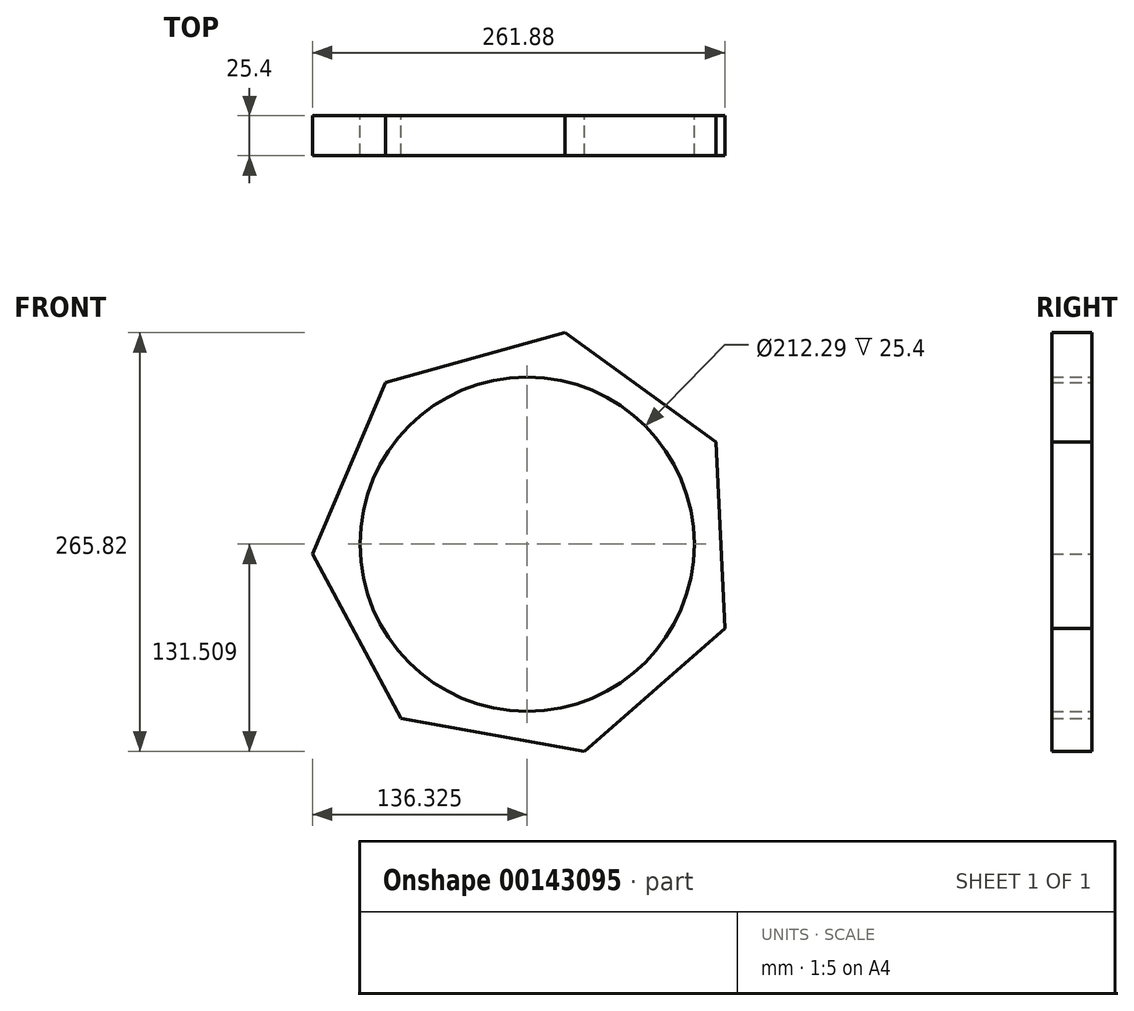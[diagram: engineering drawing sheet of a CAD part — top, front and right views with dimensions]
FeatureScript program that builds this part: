
annotation { "Feature Type Name" : "Feature", "Feature Type Description" : "" }
export const myFeature = defineFeature(function(context is Context, id is Id, definition is map)
    precondition{}
    {
        {
            var Q0;
            Q0=qCreatedBy(makeId("Front.planeOp"),FACE);
            var sketch = newSketch(context, id + "F0", { "sketchPlane" : qUnion([Q0])});
            skCircle(sketch, "E0.cCircle", {"center": v(148.42, -19.18) * mm, "radius": 122.96 * mm, "construction": true});
            skLineSegment(sketch, "E0.0", {"start": v(12.1, -25.46) * mm, "end": v(58.52, 83.5) * mm});
            skLineSegment(sketch, "E0.1", {"start": v(58.52, 83.5) * mm, "end": v(172.64, 115.13) * mm});
            skLineSegment(sketch, "E0.2", {"start": v(172.64, 115.13) * mm, "end": v(268.53, 45.63) * mm});
            skLineSegment(sketch, "E0.3", {"start": v(268.53, 45.63) * mm, "end": v(273.98, -72.68) * mm});
            skLineSegment(sketch, "E0.4", {"start": v(273.98, -72.68) * mm, "end": v(184.88, -150.7) * mm});
            skLineSegment(sketch, "E0.5", {"start": v(184.88, -150.7) * mm, "end": v(68.33, -129.68) * mm});
            skLineSegment(sketch, "E0.6", {"start": v(68.33, -129.68) * mm, "end": v(12.1, -25.46) * mm});
            skPoint(sketch, "E0.0.midPoint", {"position": v(35.3, 29.02) * mm});
            skSolve(sketch);
        }
        {
            var Q0;
            Q0=makeQuery(id+"F0.imprint","IMPRINT",FACE,{"disambiguationData":[TD([[makeQuery(id+"F0.imprint","IMPRINT",EDGE,{"derivedFrom":sQuery(id+"F0.wireOp",EDGE,"E0.0")}),-1.0]])]});
            var sketch = newSketch(context, id + "F1", { "sketchPlane" : qUnion([Q0])});
            skCircle(sketch, "E1", {"center": v(148.42, -19.18) * mm, "radius": 106.15 * mm});
            skLineSegment(sketch, "E2.0", {"start": v(58.52, 83.5) * mm, "end": v(172.64, 115.13) * mm});
            skLineSegment(sketch, "E3.0", {"start": v(172.64, 115.13) * mm, "end": v(268.53, 45.63) * mm});
            skLineSegment(sketch, "E4.0", {"start": v(268.53, 45.63) * mm, "end": v(273.98, -72.68) * mm});
            skLineSegment(sketch, "E5.0", {"start": v(273.98, -72.68) * mm, "end": v(184.88, -150.7) * mm});
            skLineSegment(sketch, "E6.0", {"start": v(184.88, -150.7) * mm, "end": v(68.33, -129.68) * mm});
            skLineSegment(sketch, "E7.0", {"start": v(68.33, -129.68) * mm, "end": v(12.1, -25.46) * mm});
            skLineSegment(sketch, "E8.0", {"start": v(12.1, -25.46) * mm, "end": v(58.52, 83.5) * mm});
            skSolve(sketch);
        }
        {
            var Q0;
            Q0 = qSketchRegion(id + "F1", true);
            extrude(context, id + "F2", {"entities" : qUnion([Q0]), "depth" : 25.4 * mm});
        }
    });
